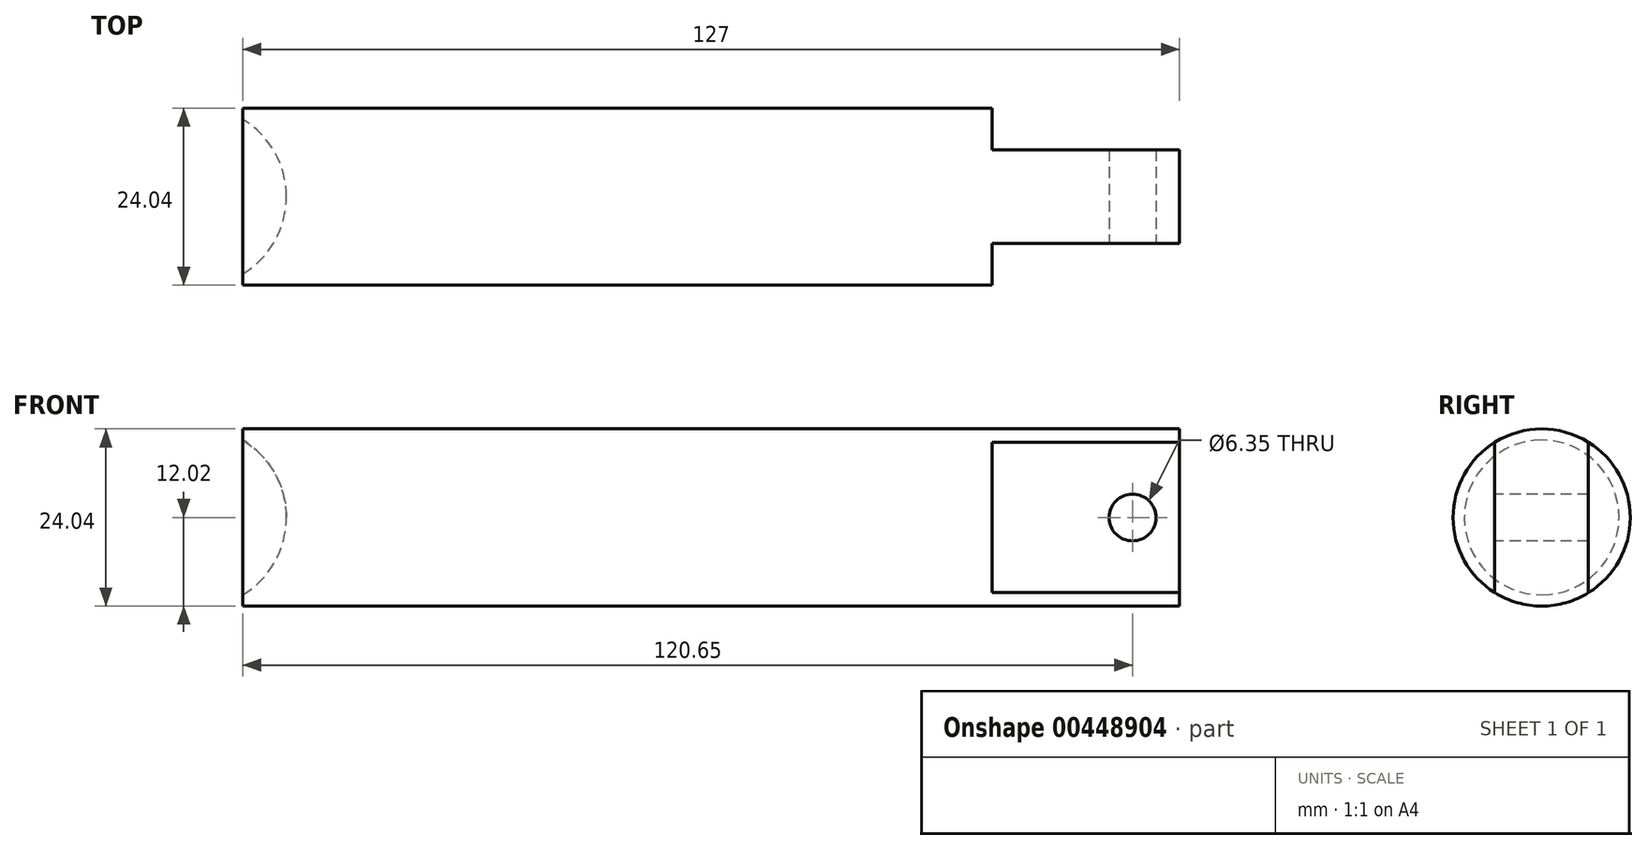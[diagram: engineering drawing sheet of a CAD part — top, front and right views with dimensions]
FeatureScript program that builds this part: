
annotation { "Feature Type Name" : "Feature", "Feature Type Description" : "" }
export const myFeature = defineFeature(function(context is Context, id is Id, definition is map)
    precondition{}
    {
        {
            var Q0;
            Q0=qCreatedBy(makeId("Front.planeOp"),FACE);
            var sketch = newSketch(context, id + "F0", { "sketchPlane" : qUnion([Q0])});
            skLineSegment(sketch, "E0", {"start": v(-120.65, 12.02) * mm, "end": v(-120.65, 10.5) * mm});
            skLineSegment(sketch, "E1", {"start": v(-120.65, 12.02) * mm, "end": v(6.35, 12.02) * mm});
            skLineSegment(sketch, "E2", {"start": v(6.35, 12.02) * mm, "end": v(6.35, 0) * mm});
            skLineSegment(sketch, "E3", {"start": v(6.35, 0) * mm, "end": v(-114.73, 0) * mm});
            skArc(sketch, "E4", {"start": v(-114.73, 0) * mm, "mid": v(-116.31, 6.02) * mm, "end": v(-120.65, 10.5) * mm});
            skSolve(sketch);
        }
        {
            var Q0;
            Q0=makeQuery(id+"F0.imprint","IMPRINT",FACE,{"disambiguationData":[TD([[makeQuery(id+"F0.imprint","IMPRINT",EDGE,{"derivedFrom":sQuery(id+"F0.wireOp",EDGE,"E0")}),1.0]])]});
            var Q1;
            Q1=sQuery(id+"F0.wireOp",EDGE,"E3");
            revolve(context, id + "F1", {"entities" : qUnion([Q0]), "axis" : qUnion([Q1]), "revolveType" : RevolveType.FULL});
        }
        {
            var Q0;
            Q0=makeQuery(id+"F1.opRevolve","SWEPT_FACE",FACE,{"disambiguationData":[OSD([sQuery(id+"F0.wireOp",EDGE,"E2")])]});
            var sketch = newSketch(context, id + "F2", { "sketchPlane" : qUnion([Q0])});
            skLineSegment(sketch, "E5", {"start": v(-6.35, 10.2) * mm, "end": v(-6.35, -10.2) * mm});
            skLineSegment(sketch, "E6", {"start": v(6.35, 10.2) * mm, "end": v(6.35, -10.2) * mm});
            skSolve(sketch);
        }
        {
            var Q0;
            Q0 = qSketchRegion(id + "F2", true);
            var Q1;
            {var subQ0=sQuery(id+"F2.wireOp",EDGE,"E5");Q1=makeQuery(id+"F2.imprint","IMPRINT",FACE,{"disambiguationData":[TD([[makeQuery(id+"F2.imprint","IMPRINT",EDGE,{"derivedFrom":subQ0}),-1.0]])]});}
            var Q2;
            {var subQ0=sQuery(id+"F2.wireOp",EDGE,"E6");Q2=makeQuery(id+"F2.imprint","IMPRINT",FACE,{"disambiguationData":[TD([[makeQuery(id+"F2.imprint","IMPRINT",EDGE,{"derivedFrom":subQ0}),1.0]])]});}
            extrude(context, id + "F3", {"entities" : qUnion([Q0, Q1, Q2]), "operationType" : NewBodyOperationType.REMOVE, "oppositeDirection" : true, "depth" : 25.4 * mm});
        }
        {
            var Q0;
            Q0=makeQuery(id+"F3.boolean.opBoolean","COPY",FACE,{"derivedFrom":makeQuery(id+"F3.opExtrude","SWEPT_FACE",FACE,{"disambiguationData":[OSD([sQuery(id+"F2.wireOp",EDGE,"E5")])]})});
            var sketch = newSketch(context, id + "F4", { "sketchPlane" : qUnion([Q0])});
            skCircle(sketch, "E7", {"center": v(0, 0) * mm, "radius": 3.18 * mm});
            skSolve(sketch);
        }
        {
            var Q0;
            Q0=makeQuery(id+"F4.imprint","IMPRINT",FACE,{"disambiguationData":[TD([[makeQuery(id+"F4.imprint","IMPRINT",EDGE,{"derivedFrom":sQuery(id+"F4.wireOp",EDGE,"E7")}),1.0]])]});
            extrude(context, id + "F5", {"entities" : qUnion([Q0]), "operationType" : NewBodyOperationType.REMOVE, "endBound" : BoundingType.THROUGH_ALL, "oppositeDirection" : true, "depth" : 25.4 * mm});
        }
    });
